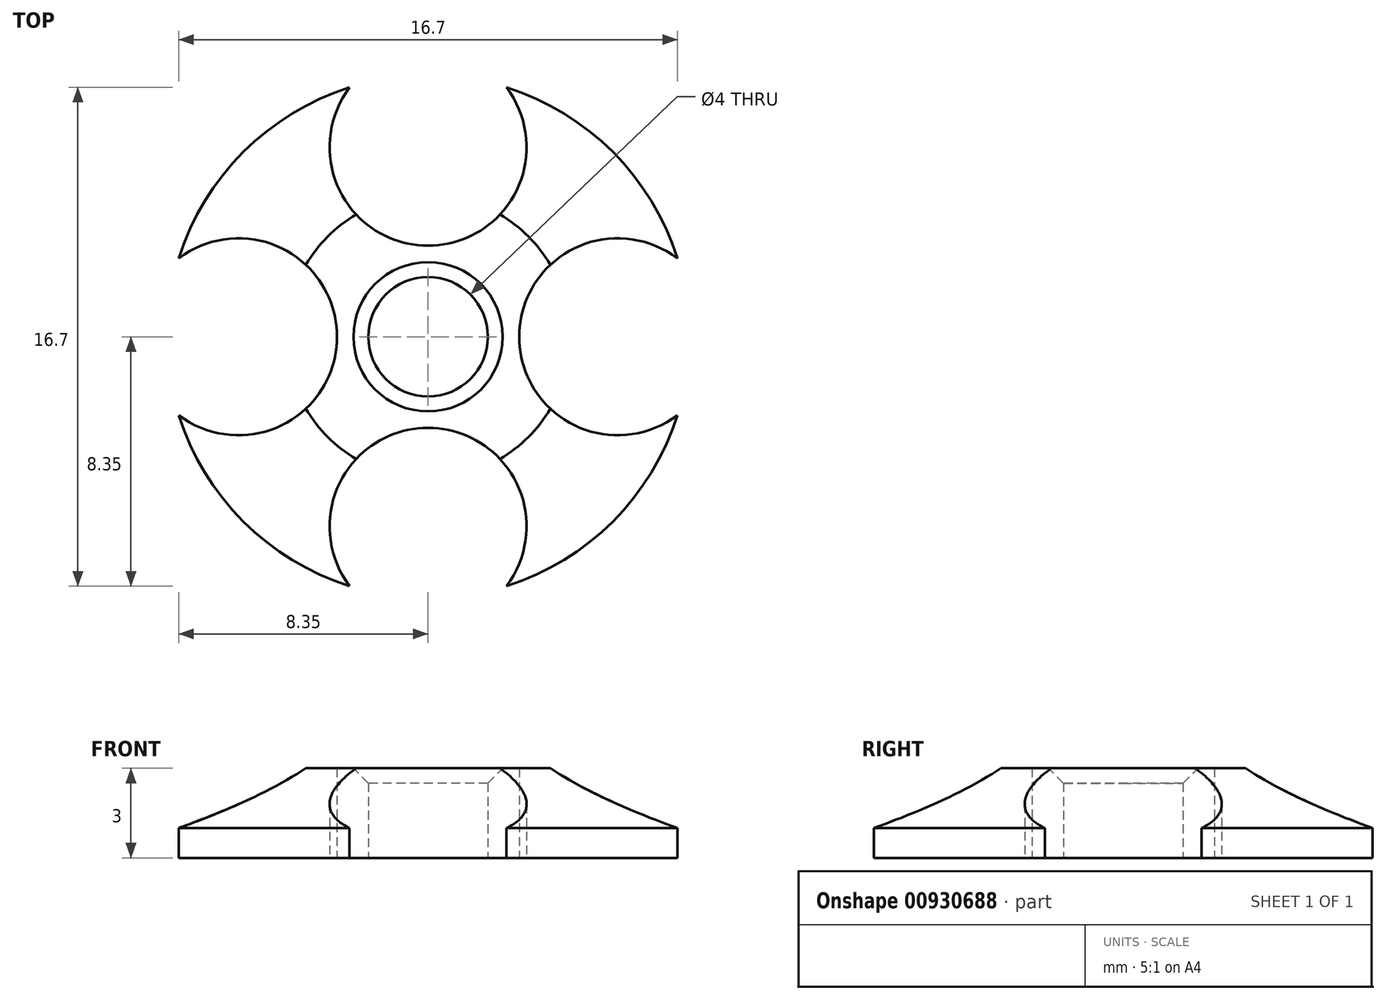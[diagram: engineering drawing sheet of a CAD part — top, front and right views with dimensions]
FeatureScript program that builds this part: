
annotation { "Feature Type Name" : "Feature", "Feature Type Description" : "" }
export const myFeature = defineFeature(function(context is Context, id is Id, definition is map)
    precondition{}
    {
        {
            var Q0;
            Q0=qCreatedBy(makeId("Top.planeOp"),FACE);
            var sketch = newSketch(context, id + "F0", { "sketchPlane" : qUnion([Q0])});
            skCircle(sketch, "E0", {"center": v(0, 0) * mm, "radius": 2 * mm});
            skCircle(sketch, "E1", {"center": v(0, 0) * mm, "radius": 6.35 * mm, "construction": true});
            skCircle(sketch, "E2", {"center": v(0, 6.35) * mm, "radius": 1.75 * mm, "construction": true});
            skCircle(sketch, "E3", {"center": v(-6.35, 0) * mm, "radius": 1.75 * mm, "construction": true});
            skCircle(sketch, "E4", {"center": v(0, -6.35) * mm, "radius": 1.75 * mm, "construction": true});
            skCircle(sketch, "E5", {"center": v(6.35, 0) * mm, "radius": 1.75 * mm, "construction": true});
            skCircle(sketch, "E6", {"center": v(0, 0) * mm, "radius": 9.35 * mm, "construction": true});
            skArc(sketch, "E7", {"start": v(-8.35, -2.63) * mm, "mid": v(-6.19, -6.19) * mm, "end": v(-2.63, -8.35) * mm});
            skArc(sketch, "E8", {"start": v(-8.35, -2.63) * mm, "mid": v(-3.05, 0) * mm, "end": v(-8.35, 2.63) * mm});
            skArc(sketch, "E9", {"start": v(-2.63, 8.35) * mm, "mid": v(0, 3.05) * mm, "end": v(2.63, 8.35) * mm});
            skArc(sketch, "E10", {"start": v(8.35, 2.63) * mm, "mid": v(3.05, 0) * mm, "end": v(8.35, -2.63) * mm});
            skArc(sketch, "E11", {"start": v(2.63, -8.35) * mm, "mid": v(0, -3.05) * mm, "end": v(-2.63, -8.35) * mm});
            skArc(sketch, "E12.trimOffspring", {"start": v(-2.63, 8.35) * mm, "mid": v(-6.19, 6.19) * mm, "end": v(-8.35, 2.63) * mm});
            skArc(sketch, "E13.trimOffspring", {"start": v(8.35, 2.63) * mm, "mid": v(6.19, 6.19) * mm, "end": v(2.63, 8.35) * mm});
            skArc(sketch, "E14.trimOffspring", {"start": v(2.63, -8.35) * mm, "mid": v(6.19, -6.19) * mm, "end": v(8.35, -2.63) * mm});
            skSolve(sketch);
        }
        {
            var Q0;
            Q0=qSketchRegion(id+"F0",true);
            extrude(context, id + "F1", {"entities" : qUnion([Q0]), "depth" : 3 * mm});
        }
        {
            var Q0;
            Q0=makeQuery(id+"F1.opExtrude","CAP_EDGE",EDGE,{"disambiguationData":[OSD([sQuery(id+"F0.wireOp",EDGE,"E12.trimOffspring")])],"isStart":false});
            var Q1;
            Q1=makeQuery(id+"F1.opExtrude","CAP_EDGE",EDGE,{"disambiguationData":[OSD([sQuery(id+"F0.wireOp",EDGE,"E7")])],"isStart":false});
            var Q2;
            Q2=makeQuery(id+"F1.opExtrude","CAP_EDGE",EDGE,{"disambiguationData":[OSD([sQuery(id+"F0.wireOp",EDGE,"E14.trimOffspring")])],"isStart":false});
            var Q3;
            Q3=makeQuery(id+"F1.opExtrude","CAP_EDGE",EDGE,{"disambiguationData":[OSD([sQuery(id+"F0.wireOp",EDGE,"E13.trimOffspring")])],"isStart":false});
            chamfer(context, id + "F2", {"entities" : qUnion([Q0, Q1, Q2, Q3]), "chamferType" : ChamferType.TWO_OFFSETS, "width1" : 4 * mm, "oppositeDirection" : false, "width2" : 2 * mm, "tangentPropagation" : true});
        }
        {
            var Q0;
            Q0=makeQuery(id+"F1.opExtrude","CAP_EDGE",EDGE,{"disambiguationData":[OSD([sQuery(id+"F0.wireOp",EDGE,"E0")])],"isStart":false});
            chamfer(context, id + "F3", {"entities" : qUnion([Q0]), "width" : 0.5 * mm, "tangentPropagation" : true});
        }
    });
